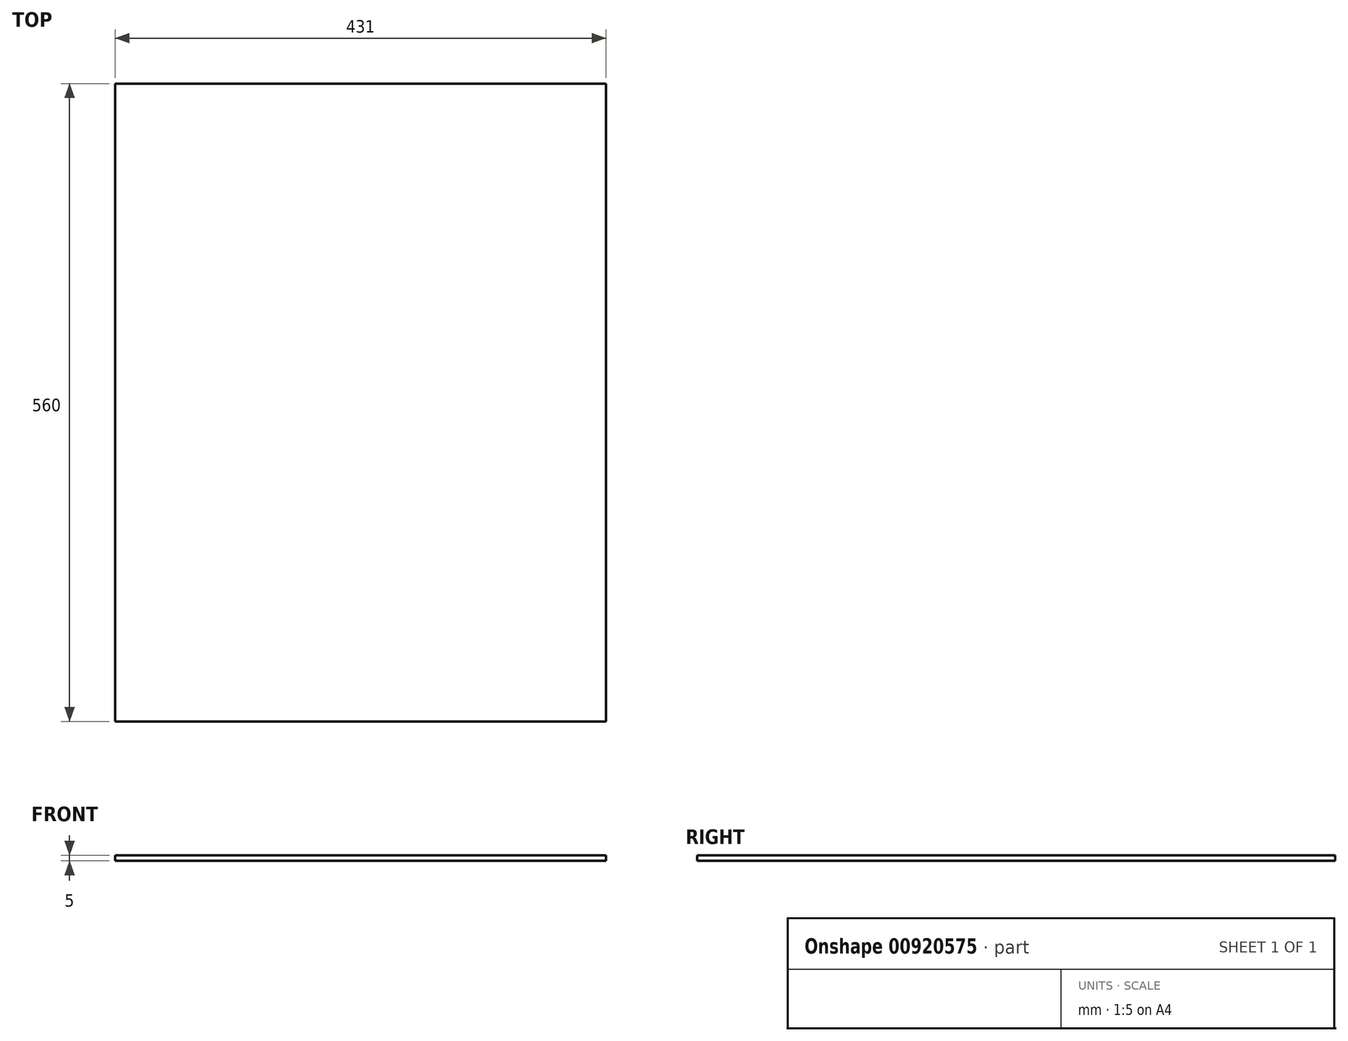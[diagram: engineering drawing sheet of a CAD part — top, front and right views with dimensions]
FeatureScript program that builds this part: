
annotation { "Feature Type Name" : "Feature", "Feature Type Description" : "" }
export const myFeature = defineFeature(function(context is Context, id is Id, definition is map)
    precondition{}
    {
        {
            var Q0;
            Q0=qCreatedBy(makeId("Top.planeOp"),FACE);
            var sketch = newSketch(context, id + "F0", { "sketchPlane" : qUnion([Q0])});
            skLineSegment(sketch, "E0.bottom", {"start": v(215.5, -280) * mm, "end": v(-215.5, -280) * mm});
            skLineSegment(sketch, "E0.top", {"start": v(215.5, 280) * mm, "end": v(-215.5, 280) * mm});
            skLineSegment(sketch, "E0.left", {"start": v(215.5, -280) * mm, "end": v(215.5, 280) * mm});
            skLineSegment(sketch, "E0.right", {"start": v(-215.5, -280) * mm, "end": v(-215.5, 280) * mm});
            skPoint(sketch, "E0.middle", {"position": v(0, 0) * mm});
            skSolve(sketch);
        }
        {
            var Q0;
            Q0=qSketchRegion(id+"F0",true);
            extrude(context, id + "F1", {"entities" : qUnion([Q0]), "depth" : 5 * mm, "symmetric" : true});
        }
    });
